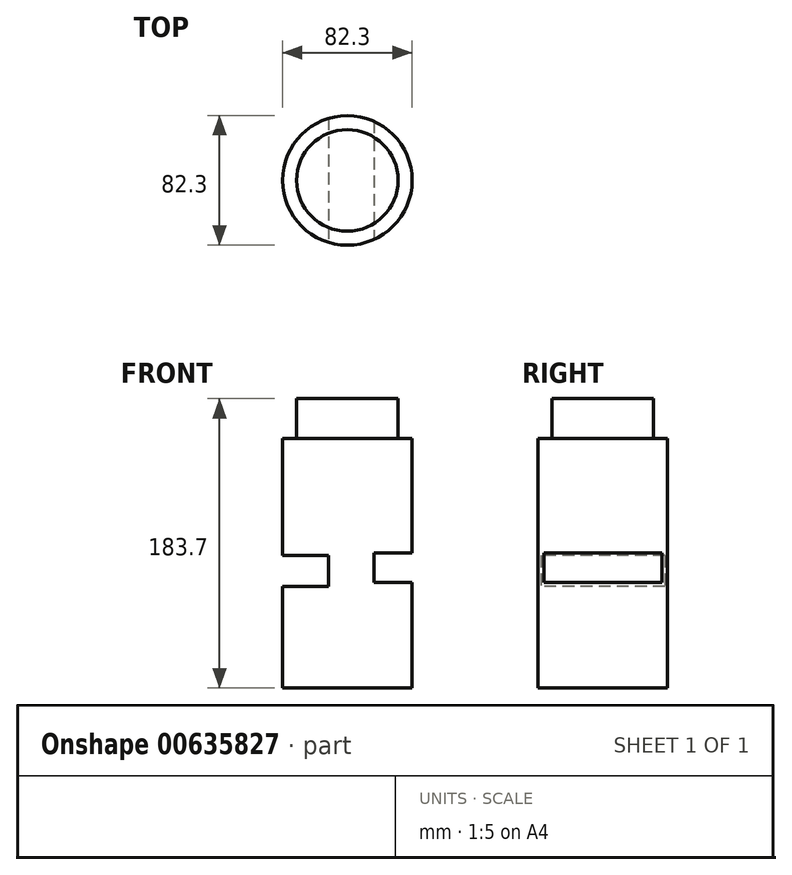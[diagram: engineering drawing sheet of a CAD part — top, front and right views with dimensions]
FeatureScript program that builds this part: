
annotation { "Feature Type Name" : "Feature", "Feature Type Description" : "" }
export const myFeature = defineFeature(function(context is Context, id is Id, definition is map)
    precondition{}
    {
        {
            var Q0;
            Q0=qCreatedBy(makeId("Top.planeOp"),FACE);
            var sketch = newSketch(context, id + "F0", { "sketchPlane" : qUnion([Q0])});
            skCircle(sketch, "E0", {"center": v(0, 0) * mm, "radius": 41.15 * mm});
            skSolve(sketch);
        }
        {
            var Q0;
            Q0 = qSketchRegion(id + "F0", true);
            extrude(context, id + "F1", {"entities" : qUnion([Q0]), "depth" : 158.3 * mm, "offsetDistance" : 25.4 * mm});
        }
        {
            var Q0;
            Q0=qCreatedBy(makeId("Front.planeOp"),FACE);
            var sketch = newSketch(context, id + "F2", { "sketchPlane" : qUnion([Q0])});
            skLineSegment(sketch, "E1.bottom", {"start": v(47.03, 85.69) * mm, "end": v(16.98, 85.69) * mm});
            skLineSegment(sketch, "E1.top", {"start": v(47.03, 66.96) * mm, "end": v(16.98, 66.96) * mm});
            skLineSegment(sketch, "E1.left", {"start": v(47.03, 85.69) * mm, "end": v(47.03, 66.96) * mm});
            skLineSegment(sketch, "E1.right", {"start": v(16.98, 85.69) * mm, "end": v(16.98, 66.96) * mm});
            skPoint(sketch, "E1.middle", {"position": v(32, 76.32) * mm});
            skSolve(sketch);
        }
        {
            var Q0;
            Q0=makeQuery(id+"F2.imprint","IMPRINT",FACE,{"disambiguationData":[TD([[makeQuery(id+"F2.imprint","IMPRINT",EDGE,{"derivedFrom":sQuery(id+"F2.wireOp",EDGE,"E1.bottom")}),1.0]])]});
            extrude(context, id + "F3", {"entities" : qUnion([Q0]), "operationType" : NewBodyOperationType.REMOVE, "endBound" : BoundingType.SYMMETRIC, "oppositeDirection" : true, "depth" : 1270 * mm, "offsetDistance" : 25.4 * mm});
        }
        {
            var Q0;
            Q0=qCreatedBy(makeId("Front.planeOp"),FACE);
            var sketch = newSketch(context, id + "F4", { "sketchPlane" : qUnion([Q0])});
            skLineSegment(sketch, "E2.bottom", {"start": v(-11.97, 84.16) * mm, "end": v(-51.38, 84.16) * mm});
            skLineSegment(sketch, "E2.top", {"start": v(-11.97, 64.35) * mm, "end": v(-51.38, 64.35) * mm});
            skLineSegment(sketch, "E2.left", {"start": v(-11.97, 84.16) * mm, "end": v(-11.97, 64.35) * mm});
            skLineSegment(sketch, "E2.right", {"start": v(-51.38, 84.16) * mm, "end": v(-51.38, 64.35) * mm});
            skSolve(sketch);
        }
        {
            var Q0;
            Q0 = qSketchRegion(id + "F4", true);
            extrude(context, id + "F5", {"entities" : qUnion([Q0]), "operationType" : NewBodyOperationType.REMOVE, "endBound" : BoundingType.SYMMETRIC, "oppositeDirection" : true, "depth" : 127 * mm, "offsetDistance" : 25.4 * mm});
        }
        {
            var Q0;
            Q0=makeQuery(id+"F1.opExtrude","CAP_FACE",FACE,{"disambiguationData":[OSD([sQuery(id+"F0.wireOp",EDGE,"E0")])],"isStart":false});
            var sketch = newSketch(context, id + "F6", { "sketchPlane" : qUnion([Q0])});
            skCircle(sketch, "E3", {"center": v(0, 0) * mm, "radius": 32.22 * mm});
            skSolve(sketch);
        }
        {
            var Q0;
            Q0 = qSketchRegion(id + "F6", true);
            extrude(context, id + "F7", {"entities" : qUnion([Q0]), "operationType" : NewBodyOperationType.ADD, "depth" : 25.4 * mm, "offsetDistance" : 25.4 * mm});
        }
    });
